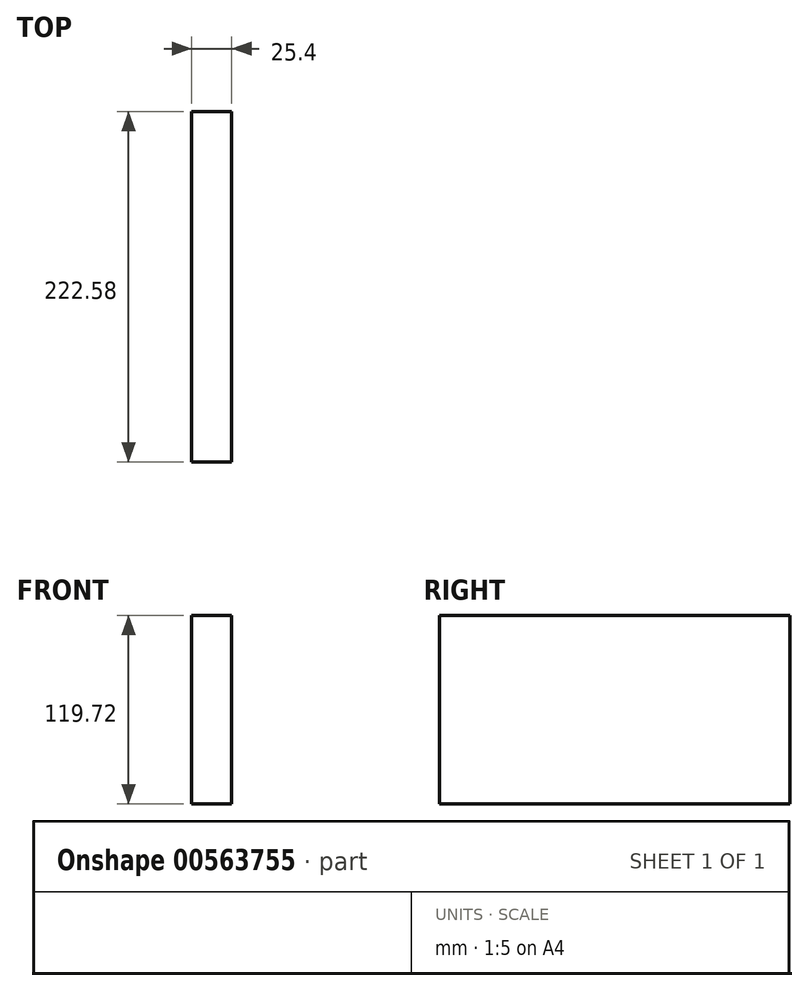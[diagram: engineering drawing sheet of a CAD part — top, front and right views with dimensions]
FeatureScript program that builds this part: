
annotation { "Feature Type Name" : "Feature", "Feature Type Description" : "" }
export const myFeature = defineFeature(function(context is Context, id is Id, definition is map)
    precondition{}
    {
        {
            var Q0;
            Q0=qCreatedBy(makeId("Right.planeOp"),FACE);
            var sketch = newSketch(context, id + "F0", { "sketchPlane" : qUnion([Q0])});
            skLineSegment(sketch, "E0.bottom", {"start": v(111.3, -59.86) * mm, "end": v(-111.3, -59.86) * mm});
            skLineSegment(sketch, "E0.top", {"start": v(111.3, 59.86) * mm, "end": v(-111.3, 59.86) * mm});
            skLineSegment(sketch, "E0.left", {"start": v(111.3, -59.86) * mm, "end": v(111.3, 59.86) * mm});
            skLineSegment(sketch, "E0.right", {"start": v(-111.3, -59.86) * mm, "end": v(-111.3, 59.86) * mm});
            skPoint(sketch, "E0.middle", {"position": v(0, 0) * mm});
            skSolve(sketch);
        }
        {
            var Q0;
            Q0 = qSketchRegion(id + "F0", true);
            extrude(context, id + "F1", {"entities" : qUnion([Q0]), "depth" : 25.4 * mm, "offsetDistance" : 25.4 * mm});
        }
    });
